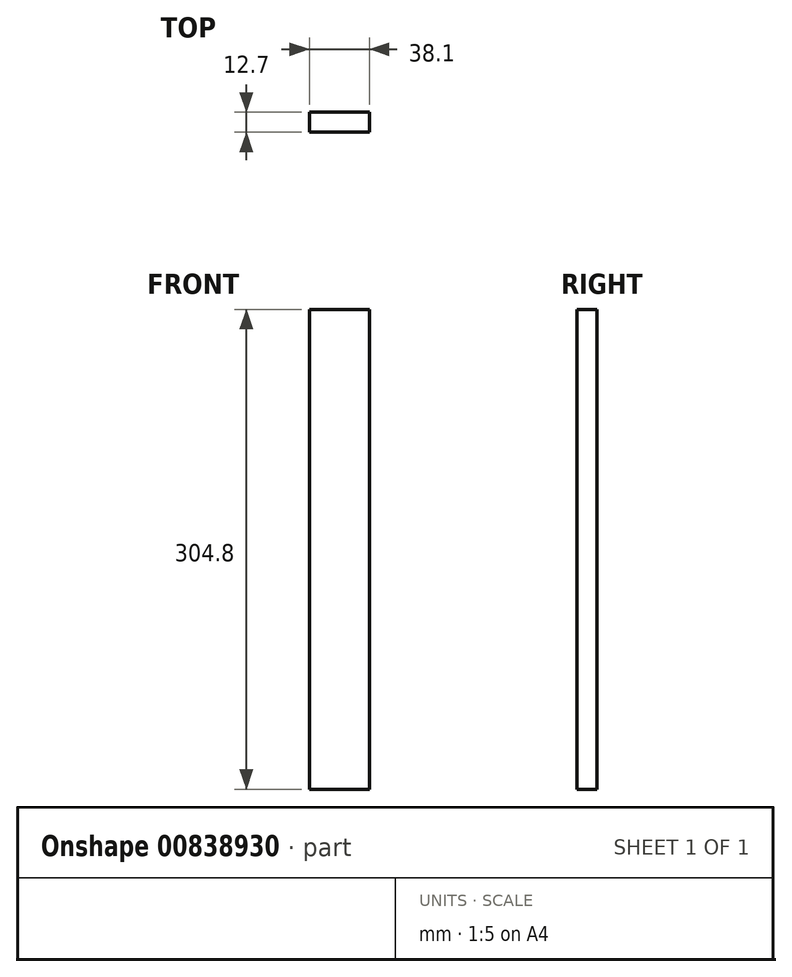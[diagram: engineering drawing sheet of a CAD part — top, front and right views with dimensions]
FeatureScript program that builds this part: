
annotation { "Feature Type Name" : "Feature", "Feature Type Description" : "" }
export const myFeature = defineFeature(function(context is Context, id is Id, definition is map)
    precondition{}
    {
        {
            var Q0;
            Q0=qCreatedBy(makeId("Front.planeOp"),FACE);
            var sketch = newSketch(context, id + "F0", { "sketchPlane" : qUnion([Q0])});
            skLineSegment(sketch, "E0", {"start": v(0, 0) * mm, "end": v(0, 304.8) * mm});
            skLineSegment(sketch, "E1", {"start": v(0, 304.8) * mm, "end": v(38.1, 304.8) * mm});
            skLineSegment(sketch, "E2", {"start": v(38.1, 304.8) * mm, "end": v(38.1, 0) * mm});
            skLineSegment(sketch, "E3", {"start": v(38.1, 0) * mm, "end": v(0, 0) * mm});
            skSolve(sketch);
        }
        {
            var Q0;
            Q0 = qSketchRegion(id + "F0", true);
            extrude(context, id + "F1", {"entities" : qUnion([Q0]), "depth" : 12.7 * mm, "offsetDistance" : 25.4 * mm});
        }
    });
